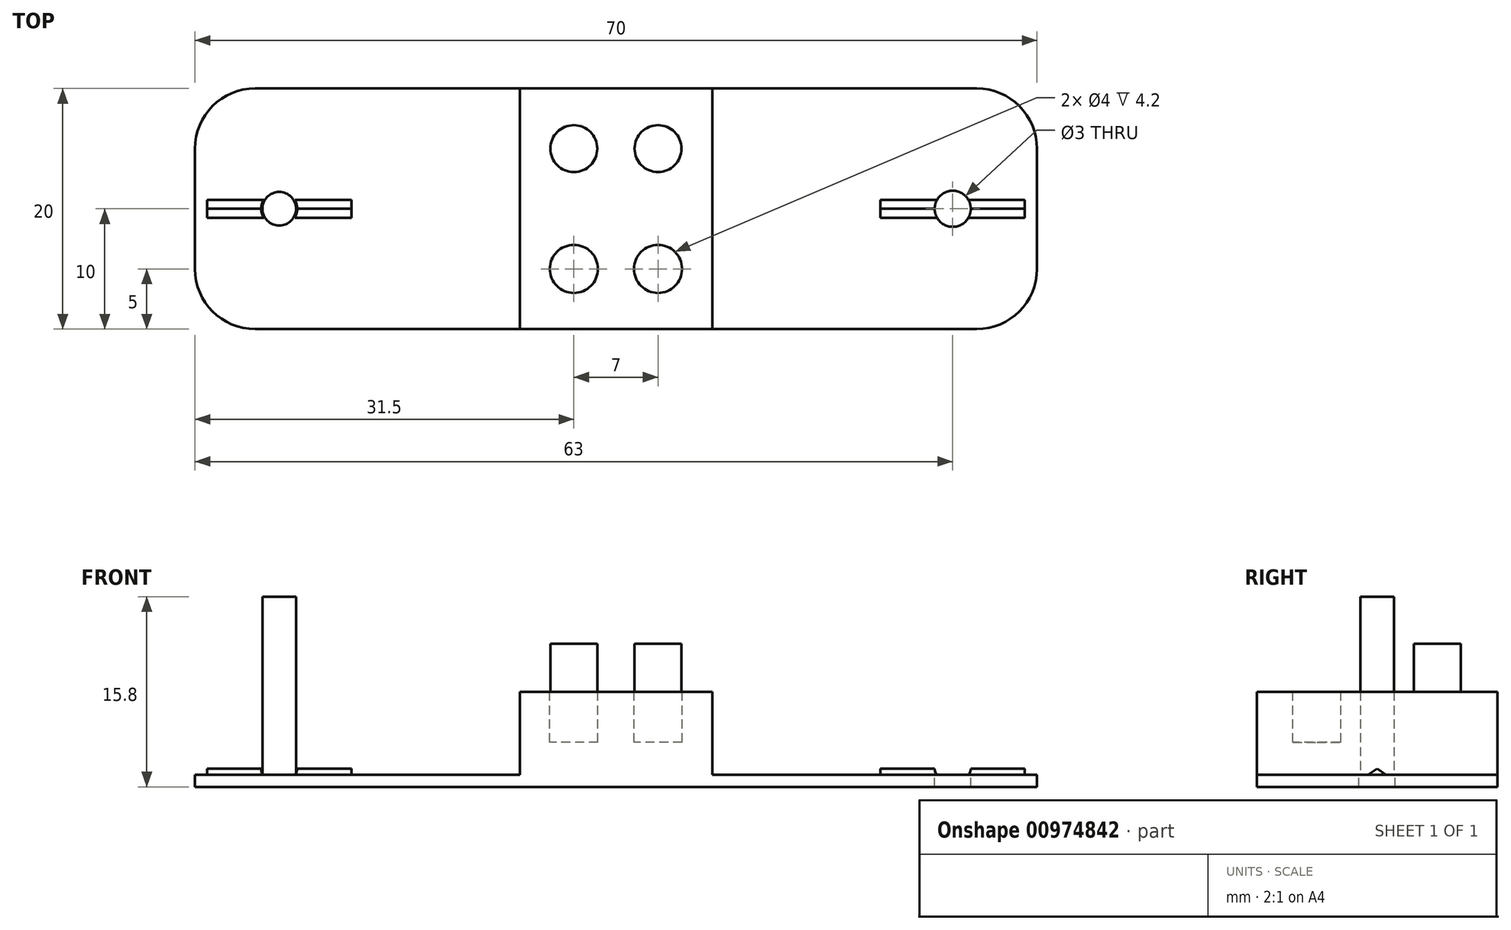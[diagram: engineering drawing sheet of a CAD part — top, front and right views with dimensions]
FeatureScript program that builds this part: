
annotation { "Feature Type Name" : "Feature", "Feature Type Description" : "" }
export const myFeature = defineFeature(function(context is Context, id is Id, definition is map)
    precondition{}
    {
        {
            var Q0;
            Q0=qCreatedBy(makeId("Top.planeOp"),FACE);
            var sketch = newSketch(context, id + "F0", { "sketchPlane" : qUnion([Q0])});
            skLineSegment(sketch, "E0.bottom", {"start": v(35, 10) * mm, "end": v(-35, 10) * mm});
            skLineSegment(sketch, "E0.top", {"start": v(35, -10) * mm, "end": v(-35, -10) * mm});
            skLineSegment(sketch, "E0.left", {"start": v(35, 10) * mm, "end": v(35, -10) * mm});
            skLineSegment(sketch, "E0.right", {"start": v(-35, 10) * mm, "end": v(-35, -10) * mm});
            skSolve(sketch);
        }
        {
            var Q0;
            Q0 = qSketchRegion(id + "F0", true);
            extrude(context, id + "F1", {"entities" : qUnion([Q0]), "depth" : 1 * mm, "offsetDistance" : 25 * mm});
        }
        {
            var Q0;
            Q0=makeQuery(id+"F1.opExtrude","CAP_FACE",FACE,{"disambiguationData":[OSD([sQuery(id+"F0.wireOp",EDGE,"E0.bottom"),sQuery(id+"F0.wireOp",EDGE,"E0.top"),sQuery(id+"F0.wireOp",EDGE,"E0.left"),sQuery(id+"F0.wireOp",EDGE,"E0.right")])],"isStart":false});
            var sketch = newSketch(context, id + "F2", { "sketchPlane" : qUnion([Q0])});
            skCircle(sketch, "E1", {"center": v(-28, 0) * mm, "radius": 1.5 * mm});
            skPoint(sketch, "E1.centerSnap0", {"position": v(-35, 0) * mm});
            skCircle(sketch, "E2", {"center": v(28, 0) * mm, "radius": 1.5 * mm});
            skPoint(sketch, "E2.centerSnap0", {"position": v(35, 0) * mm});
            skSolve(sketch);
        }
        {
            var Q0;
            Q0=sQuery(id+"F2.wireOp",VERTEX,"E1.center");
            var Q1;
            Q1=sQuery(id+"F2.wireOp",VERTEX,"E2.center");
            var Q2;
            Q2=makeQuery(id+"F1.opExtrude","SWEPT_BODY",BODY,{"disambiguationData":[OSD([sQuery(id+"F0.wireOp",EDGE,"E0.bottom"),sQuery(id+"F0.wireOp",EDGE,"E0.top"),sQuery(id+"F0.wireOp",EDGE,"E0.left"),sQuery(id+"F0.wireOp",EDGE,"E0.right")])]});
            hole(context, id + "F3", {"style" : HoleStyle.SIMPLE, "endStyle" : HoleEndStyle.THROUGH, "holeDiameter" : 3 * mm, "majorDiameter" : 5 * mm, "isTappedThrough" : true, "tappedDepth" : 12 * mm, "tapClearance" : 3, "locations" : qUnion([Q0, Q1]), "scope" : qUnion([Q2])});
        }
        {
            var Q0;
            Q0=makeQuery(id+"F1.opExtrude","SWEPT_EDGE",EDGE,{"disambiguationData":[OSD([sQuery(id+"F0.wireOp",EDGE,"E0.bottom"),sQuery(id+"F0.wireOp",EDGE,"E0.right")])]});
            var Q1;
            Q1=makeQuery(id+"F1.opExtrude","SWEPT_EDGE",EDGE,{"disambiguationData":[OSD([sQuery(id+"F0.wireOp",EDGE,"E0.top"),sQuery(id+"F0.wireOp",EDGE,"E0.right")])]});
            var Q2;
            Q2=makeQuery(id+"F1.opExtrude","SWEPT_EDGE",EDGE,{"disambiguationData":[OSD([sQuery(id+"F0.wireOp",EDGE,"E0.bottom"),sQuery(id+"F0.wireOp",EDGE,"E0.left")])]});
            var Q3;
            Q3=makeQuery(id+"F1.opExtrude","SWEPT_EDGE",EDGE,{"disambiguationData":[OSD([sQuery(id+"F0.wireOp",EDGE,"E0.top"),sQuery(id+"F0.wireOp",EDGE,"E0.left")])]});
            fillet(context, id + "F4", {"entities" : qUnion([Q0, Q1, Q2, Q3]), "radius" : 5 * mm, "tangentPropagation" : true, "allowEdgeOverflow" : false});
        }
        {
            var Q0;
            Q0=makeQuery(id+"F1.opExtrude","CAP_FACE",FACE,{"disambiguationData":[OSD([sQuery(id+"F0.wireOp",EDGE,"E0.bottom"),sQuery(id+"F0.wireOp",EDGE,"E0.top"),sQuery(id+"F0.wireOp",EDGE,"E0.left"),sQuery(id+"F0.wireOp",EDGE,"E0.right")])],"isStart":false});
            var sketch = newSketch(context, id + "F5", { "sketchPlane" : qUnion([Q0])});
            skLineSegment(sketch, "E3", {"start": v(-34, 0.75) * mm, "end": v(-29.3, 0.75) * mm});
            skLineSegment(sketch, "E4", {"start": v(-22, 0.75) * mm, "end": v(-22, -0.75) * mm});
            skLineSegment(sketch, "E5", {"start": v(-22, -0.75) * mm, "end": v(-26.7, -0.75) * mm});
            skLineSegment(sketch, "E6", {"start": v(-34, -0.75) * mm, "end": v(-34, 0.75) * mm});
            skArc(sketch, "E7", {"start": v(-29.3, 0.75) * mm, "mid": v(-29.5, 0) * mm, "end": v(-29.3, -0.75) * mm});
            skLineSegment(sketch, "E8.trimOffspring", {"start": v(-26.7, 0.75) * mm, "end": v(-22, 0.75) * mm});
            skLineSegment(sketch, "E9.trimOffspring", {"start": v(-29.3, -0.75) * mm, "end": v(-34, -0.75) * mm});
            skArc(sketch, "E10.trimOffspring", {"start": v(-26.7, -0.75) * mm, "mid": v(-26.5, 0) * mm, "end": v(-26.7, 0.75) * mm});
            skSolve(sketch);
        }
        {
            var Q0;
            Q0=makeQuery(id+"F1.opExtrude","CAP_FACE",FACE,{"disambiguationData":[OSD([sQuery(id+"F0.wireOp",EDGE,"E0.bottom"),sQuery(id+"F0.wireOp",EDGE,"E0.top"),sQuery(id+"F0.wireOp",EDGE,"E0.left"),sQuery(id+"F0.wireOp",EDGE,"E0.right")])],"isStart":false});
            var sketch = newSketch(context, id + "F6", { "sketchPlane" : qUnion([Q0])});
            skLineSegment(sketch, "E11", {"start": v(22, 0.75) * mm, "end": v(26.7, 0.75) * mm});
            skLineSegment(sketch, "E12", {"start": v(34, 0.75) * mm, "end": v(34, -0.75) * mm});
            skLineSegment(sketch, "E13", {"start": v(34, -0.75) * mm, "end": v(29.3, -0.75) * mm});
            skLineSegment(sketch, "E14", {"start": v(22, -0.75) * mm, "end": v(22, 0.75) * mm});
            skArc(sketch, "E15", {"start": v(26.7, 0.75) * mm, "mid": v(26.5, 0) * mm, "end": v(26.7, -0.75) * mm});
            skLineSegment(sketch, "E16.trimOffspring", {"start": v(29.3, 0.75) * mm, "end": v(34, 0.75) * mm});
            skLineSegment(sketch, "E17.trimOffspring", {"start": v(26.7, -0.75) * mm, "end": v(22, -0.75) * mm});
            skArc(sketch, "E18.trimOffspring", {"start": v(29.3, -0.75) * mm, "mid": v(29.5, 0) * mm, "end": v(29.3, 0.75) * mm});
            skSolve(sketch);
        }
        {
            var Q0;
            Q0=makeQuery(id+"F5.imprint","IMPRINT",FACE,{"disambiguationData":[TD([[makeQuery(id+"F5.imprint","IMPRINT",EDGE,{"derivedFrom":sQuery(id+"F5.wireOp",EDGE,"E3")}),-1.0]])]});
            var Q1;
            Q1=makeQuery(id+"F5.imprint","IMPRINT",FACE,{"disambiguationData":[TD([[makeQuery(id+"F5.imprint","IMPRINT",EDGE,{"derivedFrom":sQuery(id+"F5.wireOp",EDGE,"E4")}),-1.0]])]});
            var Q2;
            Q2=makeQuery(id+"F6.imprint","IMPRINT",FACE,{"disambiguationData":[TD([[makeQuery(id+"F6.imprint","IMPRINT",EDGE,{"derivedFrom":sQuery(id+"F6.wireOp",EDGE,"E11")}),-1.0]])]});
            var Q3;
            Q3=makeQuery(id+"F6.imprint","IMPRINT",FACE,{"disambiguationData":[TD([[makeQuery(id+"F6.imprint","IMPRINT",EDGE,{"derivedFrom":sQuery(id+"F6.wireOp",EDGE,"E12")}),-1.0]])]});
            extrude(context, id + "F7", {"entities" : qUnion([Q0, Q1, Q2, Q3]), "operationType" : NewBodyOperationType.ADD, "depth" : 0.5 * mm, "offsetDistance" : 25 * mm});
        }
        {
            var Q0;
            Q0=makeQuery(id+"F7.opExtrude","SWEPT_FACE",FACE,{"disambiguationData":[OSD([sQuery(id+"F5.wireOp",EDGE,"E6")])]});
            var sketch = newSketch(context, id + "F8", { "sketchPlane" : qUnion([Q0])});
            skLineSegment(sketch, "E19", {"start": v(-0.75, 1) * mm, "end": v(0, 1.5) * mm});
            skLineSegment(sketch, "E20", {"start": v(0, 1.5) * mm, "end": v(0.75, 1) * mm});
            skLineSegment(sketch, "E21", {"start": v(0.75, 1) * mm, "end": v(-0.75, 1) * mm});
            skSolve(sketch);
        }
        {
            var Q0;
            {var subQ0=sQuery(id+"F8.wireOp",EDGE,"E19");Q0=makeQuery(id+"F8.imprint","IMPRINT",FACE,{"disambiguationData":[TD([[makeQuery(id+"F8.imprint","IMPRINT",EDGE,{"derivedFrom":subQ0}),1.0]])]});}
            var Q1;
            {var subQ0=sQuery(id+"F8.wireOp",EDGE,"E20");Q1=makeQuery(id+"F8.imprint","IMPRINT",FACE,{"disambiguationData":[TD([[makeQuery(id+"F8.imprint","IMPRINT",EDGE,{"derivedFrom":subQ0}),1.0]])]});}
            extrude(context, id + "F9", {"entities" : qUnion([Q0, Q1]), "operationType" : NewBodyOperationType.REMOVE, "endBound" : BoundingType.THROUGH_ALL, "oppositeDirection" : true, "depth" : 25 * mm, "offsetDistance" : 25 * mm});
        }
        {
            var Q0;
            Q0=makeQuery(id+"F1.opExtrude","CAP_FACE",FACE,{"disambiguationData":[OSD([sQuery(id+"F0.wireOp",EDGE,"E0.bottom"),sQuery(id+"F0.wireOp",EDGE,"E0.top"),sQuery(id+"F0.wireOp",EDGE,"E0.left"),sQuery(id+"F0.wireOp",EDGE,"E0.right")])],"isStart":false});
            var sketch = newSketch(context, id + "F10", { "sketchPlane" : qUnion([Q0])});
            skLineSegment(sketch, "E22.bottom", {"start": v(-8, -10) * mm, "end": v(8, -10) * mm});
            skLineSegment(sketch, "E22.top", {"start": v(-8, 10) * mm, "end": v(8, 10) * mm});
            skLineSegment(sketch, "E22.left", {"start": v(-8, -10) * mm, "end": v(-8, 10) * mm});
            skLineSegment(sketch, "E22.right", {"start": v(8, -10) * mm, "end": v(8, 10) * mm});
            skPoint(sketch, "E22.middle", {"position": v(0, 0) * mm});
            skSolve(sketch);
        }
        {
            var Q0;
            Q0=makeQuery(id+"F10.imprint","IMPRINT",FACE,{"disambiguationData":[TD([[makeQuery(id+"F10.imprint","IMPRINT",EDGE,{"derivedFrom":sQuery(id+"F10.wireOp",EDGE,"E22.bottom")}),-1.0]])]});
            extrude(context, id + "F11", {"entities" : qUnion([Q0]), "operationType" : NewBodyOperationType.ADD, "depth" : 6.9 * mm, "offsetDistance" : 25 * mm});
        }
        {
            var Q0;
            Q0=makeQuery(id+"F11.opExtrude","CAP_FACE",FACE,{"disambiguationData":[OSD([sQuery(id+"F10.wireOp",EDGE,"E22.bottom"),sQuery(id+"F10.wireOp",EDGE,"E22.top"),sQuery(id+"F10.wireOp",EDGE,"E22.left"),sQuery(id+"F10.wireOp",EDGE,"E22.right")])],"isStart":false});
            var sketch = newSketch(context, id + "F12", { "sketchPlane" : qUnion([Q0])});
            skCircle(sketch, "E23", {"center": v(-3.5, 5) * mm, "radius": 1.95 * mm});
            skCircle(sketch, "E24", {"center": v(3.5, 5) * mm, "radius": 1.95 * mm});
            skCircle(sketch, "E25", {"center": v(-3.5, -5) * mm, "radius": 2 * mm});
            skCircle(sketch, "E26", {"center": v(3.5, -5) * mm, "radius": 2 * mm});
            skSolve(sketch);
        }
        {
            var Q0;
            Q0=makeQuery(id+"F12.imprint","IMPRINT",FACE,{"disambiguationData":[TD([[makeQuery(id+"F12.imprint","IMPRINT",EDGE,{"derivedFrom":sQuery(id+"F12.wireOp",EDGE,"E23")}),1.0]])]});
            var Q1;
            Q1=makeQuery(id+"F12.imprint","IMPRINT",FACE,{"disambiguationData":[TD([[makeQuery(id+"F12.imprint","IMPRINT",EDGE,{"derivedFrom":sQuery(id+"F12.wireOp",EDGE,"E24")}),1.0]])]});
            extrude(context, id + "F13", {"entities" : qUnion([Q0, Q1]), "operationType" : NewBodyOperationType.ADD, "depth" : 4 * mm, "offsetDistance" : 25 * mm});
        }
        {
            var Q0;
            Q0=makeQuery(id+"F11.opExtrude","CAP_FACE",FACE,{"disambiguationData":[OSD([sQuery(id+"F10.wireOp",EDGE,"E22.bottom"),sQuery(id+"F10.wireOp",EDGE,"E22.top"),sQuery(id+"F10.wireOp",EDGE,"E22.left"),sQuery(id+"F10.wireOp",EDGE,"E22.right")])],"isStart":false});
            var sketch = newSketch(context, id + "F14", { "sketchPlane" : qUnion([Q0])});
            skCircle(sketch, "E27", {"center": v(-3.5, 5) * mm, "radius": 1.95 * mm});
            skCircle(sketch, "E28", {"center": v(3.5, 5) * mm, "radius": 1.95 * mm});
            skCircle(sketch, "E29", {"center": v(-3.5, -5) * mm, "radius": 2 * mm});
            skCircle(sketch, "E30", {"center": v(3.5, -5) * mm, "radius": 2 * mm});
            skSolve(sketch);
        }
        {
            var Q0;
            Q0=makeQuery(id+"F14.imprint","IMPRINT",FACE,{"disambiguationData":[TD([[makeQuery(id+"F14.imprint","IMPRINT",EDGE,{"derivedFrom":sQuery(id+"F14.wireOp",EDGE,"E29")}),1.0]])]});
            var Q1;
            Q1=makeQuery(id+"F14.imprint","IMPRINT",FACE,{"disambiguationData":[TD([[makeQuery(id+"F14.imprint","IMPRINT",EDGE,{"derivedFrom":sQuery(id+"F14.wireOp",EDGE,"E30")}),1.0]])]});
            extrude(context, id + "F15", {"entities" : qUnion([Q0, Q1]), "operationType" : NewBodyOperationType.REMOVE, "oppositeDirection" : true, "depth" : 4.2 * mm, "offsetDistance" : 25 * mm});
        }
        {
            var Q0;
            {var subQ2=sQuery(id+"F0.wireOp",EDGE,"E0.right");var subQ3=sQuery(id+"F0.wireOp",EDGE,"E0.top");var subQ5=sQuery(id+"F0.wireOp",EDGE,"E0.bottom");var subQ9=makeQuery(id+"F1.opExtrude","CAP_FACE",FACE,{"disambiguationData":[OSD([subQ5,subQ3,sQuery(id+"F0.wireOp",EDGE,"E0.left"),subQ2])],"isStart":false});Q0=makeQuery(id+"F11.boolean.opBoolean","SPLIT",FACE,{"disambiguationData":[TD([makeQuery(id+"F1.opExtrude","SWEPT_FACE",FACE,{"disambiguationData":[OSD([subQ2])]})])],"derivedFrom":subQ9});}
            var sketch = newSketch(context, id + "F16", { "sketchPlane" : qUnion([Q0])});
            skCircle(sketch, "E31", {"center": v(-28, 0) * mm, "radius": 1.5 * mm});
            skSolve(sketch);
        }
        {
            var Q0;
            Q0 = qSketchRegion(id + "F16", true);
            extrude(context, id + "F17", {"entities" : qUnion([Q0]), "operationType" : NewBodyOperationType.ADD, "oppositeDirection" : true, "depth" : 1 * mm, "offsetDistance" : 25 * mm});
        }
        {
            var Q0;
            {var subQ2=sQuery(id+"F0.wireOp",EDGE,"E0.right");var subQ3=sQuery(id+"F0.wireOp",EDGE,"E0.top");var subQ5=sQuery(id+"F0.wireOp",EDGE,"E0.bottom");var subQ9=makeQuery(id+"F1.opExtrude","CAP_FACE",FACE,{"disambiguationData":[OSD([subQ5,subQ3,sQuery(id+"F0.wireOp",EDGE,"E0.left"),subQ2])],"isStart":false});Q0=makeQuery(id+"F17.boolean.opBoolean","MERGE",FACE,{"derivedFrom":[makeQuery(id+"F11.boolean.opBoolean","SPLIT",FACE,{"disambiguationData":[TD([makeQuery(id+"F1.opExtrude","SWEPT_FACE",FACE,{"disambiguationData":[OSD([subQ2])]})])],"derivedFrom":subQ9}),makeQuery(id+"F17.opExtrude","CAP_FACE",FACE,{"disambiguationData":[OSD([sQuery(id+"F16.wireOp",EDGE,"E31")])],"isStart":true})]});}
            var sketch = newSketch(context, id + "F18", { "sketchPlane" : qUnion([Q0])});
            skCircle(sketch, "E32", {"center": v(-28, 0) * mm, "radius": 1.4 * mm});
            skSolve(sketch);
        }
        {
            var Q0;
            Q0 = qSketchRegion(id + "F18", true);
            extrude(context, id + "F19", {"entities" : qUnion([Q0]), "operationType" : NewBodyOperationType.ADD, "depth" : 14.8 * mm, "offsetDistance" : 25 * mm});
        }
    });
